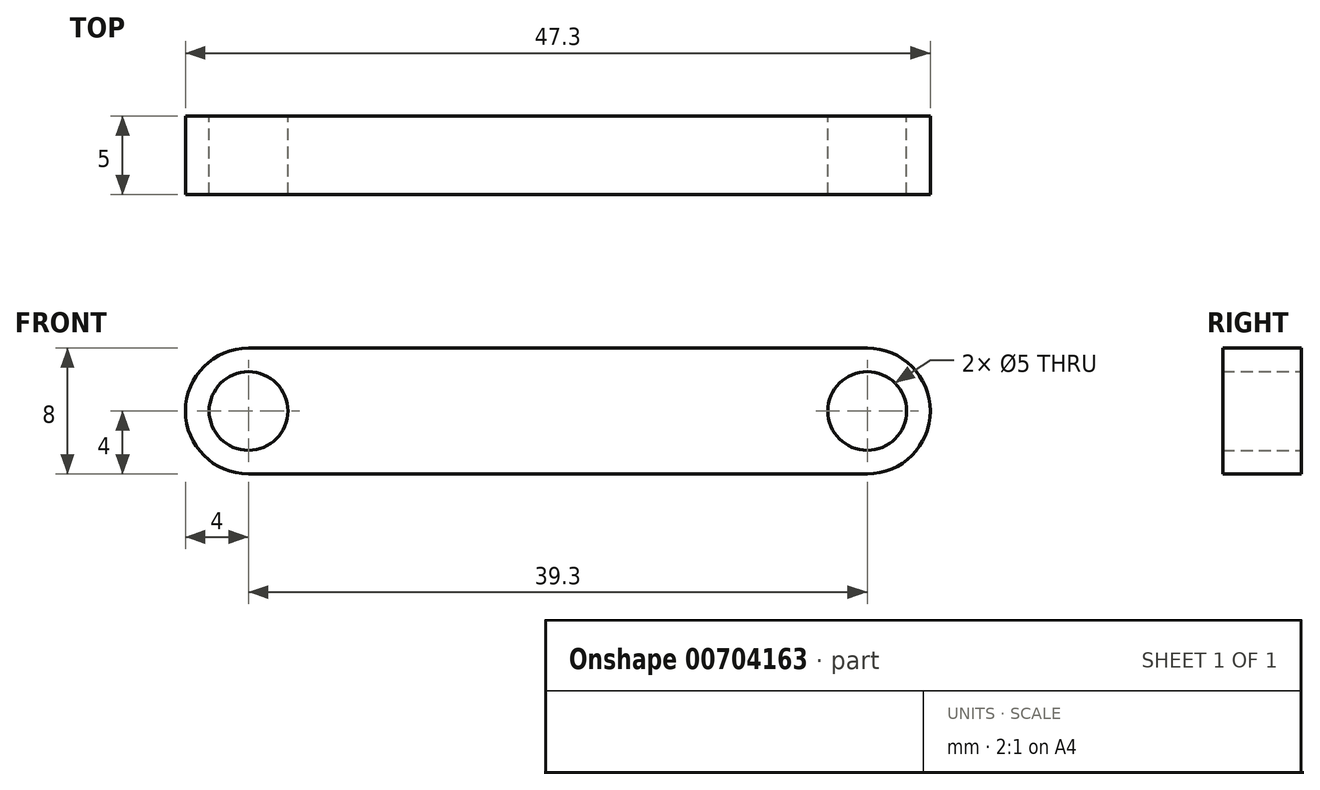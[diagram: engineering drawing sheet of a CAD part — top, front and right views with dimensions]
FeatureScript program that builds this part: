
annotation { "Feature Type Name" : "Feature", "Feature Type Description" : "" }
export const myFeature = defineFeature(function(context is Context, id is Id, definition is map)
    precondition{}
    {
        {
            var Q0;
            Q0=qCreatedBy(makeId("Front.planeOp"),FACE);
            var sketch = newSketch(context, id + "F0", { "sketchPlane" : qUnion([Q0])});
            skLineSegment(sketch, "E0.bottom", {"start": v(-19.65, 4) * mm, "end": v(0, 4) * mm});
            skLineSegment(sketch, "E0.top", {"start": v(-19.65, -4) * mm, "end": v(0, -4) * mm});
            skLineSegment(sketch, "E0.left", {"start": v(-19.65, 4) * mm, "end": v(-19.65, -4) * mm, "construction": true});
            skLineSegment(sketch, "E0.right", {"start": v(0, 4) * mm, "end": v(0, -4) * mm});
            skArc(sketch, "E1", {"start": v(-19.65, -4) * mm, "mid": v(-23.65, 0) * mm, "end": v(-19.65, 4) * mm});
            skCircle(sketch, "E2", {"center": v(-19.65, 0) * mm, "radius": 2.5 * mm});
            skLineSegment(sketch, "E3.MirrorCS", {"start": v(19.65, -4) * mm, "end": v(0, -4) * mm});
            skArc(sketch, "E4.MirrorCS", {"start": v(19.65, -4) * mm, "mid": v(23.65, 0) * mm, "end": v(19.65, 4) * mm});
            skCircle(sketch, "E5.MirrorC", {"center": v(19.65, 0) * mm, "radius": 2.5 * mm});
            skLineSegment(sketch, "E6.MirrorCS", {"start": v(19.65, 4) * mm, "end": v(0, 4) * mm});
            skSolve(sketch);
        }
        {
            var Q0;
            Q0=makeQuery(id+"F0.imprint","IMPRINT",FACE,{"disambiguationData":[TD([[makeQuery(id+"F0.imprint","IMPRINT",EDGE,{"derivedFrom":sQuery(id+"F0.wireOp",EDGE,"E0.bottom")}),-1.0]])]});
            var Q1;
            Q1=makeQuery(id+"F0.imprint","IMPRINT",FACE,{"disambiguationData":[TD([[makeQuery(id+"F0.imprint","IMPRINT",EDGE,{"derivedFrom":sQuery(id+"F0.wireOp",EDGE,"E0.right")}),1.0]])]});
            extrude(context, id + "F1", {"entities" : qUnion([Q0, Q1]), "depth" : 5 * mm, "offsetDistance" : 25 * mm});
        }
    });
